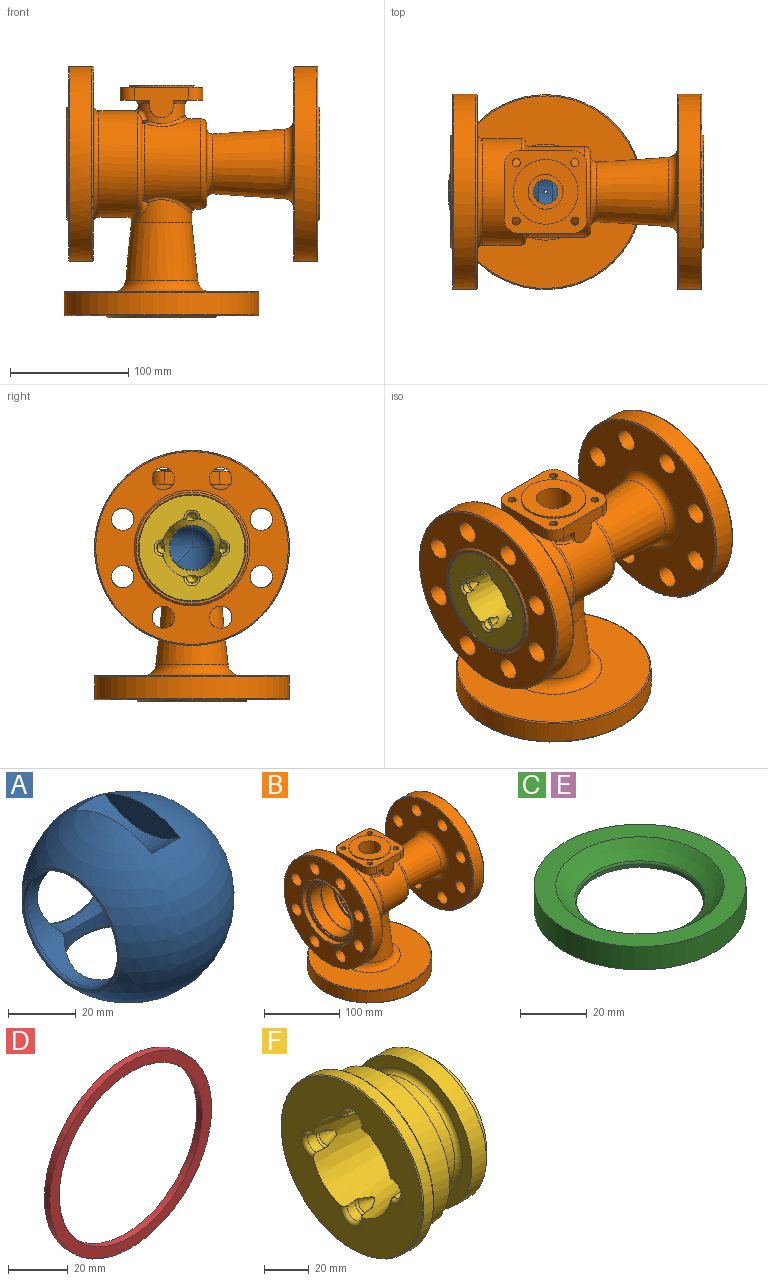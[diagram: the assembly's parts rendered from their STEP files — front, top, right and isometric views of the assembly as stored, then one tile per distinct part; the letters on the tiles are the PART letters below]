
ASSEMBLY  parts=6 mates=11
PART A: 15 faces, bbox 63x63x55.2 mm
  f0: sphere r=19mm, area 565.3mm2, adj f2,f3,f7,f14
  f1: cylinder r=25.4mm len=32.65mm, axis (1,0,0), area 413.6mm2, adj f4,f5,f6,f14
  f2: cylinder r=19mm len=38mm, axis (1,0,0), area 1522.5mm2, adj f0,f3,f7,f11,f14
  f3: cylinder r=19mm len=38mm, axis (0,1,0), area 1540.4mm2, adj f0,f2,f7,f10,f14
  f4: sphere r=31.5mm, area 7592mm2, adj f1,f5,f6,f9,f12,f13
  f5: plane 31.7x9.92mm, normal (1,0,0), area 213.9mm2, adj f1,f4
  f6: plane 31.7x9.92mm, normal (-1,0,0), area 213.9mm2, adj f1,f4
  f7: cylinder r=19mm len=38mm, axis (0,0,1), area 1543.1mm2, adj f0,f2,f3,f8
  f8: torus R=20mm, axis (0,0,1), area 103.9mm2, adj f7,f9
  f9: torus R=19.87mm, axis (0,0,-1), area 140.8mm2, adj f4,f8
  f10: torus R=20mm, axis (0,-1,0), area 103.9mm2, adj f3,f12
  f11: torus R=20mm, axis (1,0,0), area 185mm2, adj f2,f13
  f12: torus R=19.87mm, axis (0,1,0), area 140.8mm2, adj f4,f10
  f13: torus R=19.99mm, axis (-1,0,0), area 77.1mm2, adj f4,f11
  f14: cylinder r=1.5mm len=3mm, axis (0,0,-1), area 19.2mm2, adj f0,f1,f2,f3
PART B: 128 faces, bbox 239.3x194.7x235.4 mm
  f0: plane 163.1x163.1mm, normal (1,0,0), area 11081.7mm2, adj f41,f50,f114,f115,f116,f117,f118,f119
  f1: plane 163.1x163.1mm, normal (-1,0,0), area 14231.2mm2, adj f43,f51,f114,f115,f116,f117,f118,f119
  f2: plane 70x25mm, normal (0,0,-1), area 1229.7mm2, adj f9,f13,f14,f15,f16,f100,f104,f122
  f3: cylinder r=20mm len=40mm, axis (0,0,1), area 1013mm2, adj f75,f78,f81,f82,f100,f101,f102,f103
  f4: torus R=41mm, axis (1,0,0), area 611.2mm2, adj f18,f19,f75,f94
  f5: cylinder r=38.25mm len=76.5mm, axis (-1,0,0), area 7907mm2, adj f7,f47,f52,f73,f80,f81,f85,f86
  f6: plane 83.81x38.56mm, normal (1,0,0), area 59.6mm2, adj f7,f17,f79,f93
  f7: torus R=40.25mm, axis (1,0,0), area 238mm2, adj f5,f6,f80,f87
  f8: cylinder r=31.8mm len=63.6mm, axis (-1,0,0), area 9275.5mm2, adj f34,f35,f58,f69
  f9: plane 46x26mm, normal (0,1,0), area 763.1mm2, adj f2,f10,f16,f53,f55,f103,f104,f105
  f10: cylinder r=12mm len=12mm, axis (0,0,1), area 207.3mm2, adj f9,f11,f53,f55
  f11: plane 46x11mm, normal (-1,0,0), area 506mm2, adj f10,f12,f53,f55
  f12: cylinder r=12mm len=12mm, axis (0,0,1), area 207.3mm2, adj f11,f13,f53,f55
  f13: plane 46x26mm, normal (0,-1,0), area 763.1mm2, adj f2,f12,f14,f53,f55,f100,f101,f102
  f14: cylinder r=12mm len=12mm, axis (0,0,1), area 207.3mm2, adj f2,f13,f15,f55
  f15: plane 46x11mm, normal (1,0,0), area 506mm2, adj f2,f14,f16,f55
  f16: cylinder r=12mm len=12mm, axis (0,0,1), area 207.3mm2, adj f2,f9,f15,f55
  f17: torus R=41mm, axis (1,0,0), area 1154.6mm2, adj f6,f19,f82,f95
  f18: plane 67.81x22.56mm, normal (1,0,0), area 59.6mm2, adj f4,f52,f74,f88
  f19: cylinder r=45mm len=90mm, axis (-1,0,0), area 9132.6mm2, adj f4,f17,f78,f96,f99
  f20: plane 163.1x163.1mm, normal (1,0,0), area 10770.6mm2, adj f48,f99,f106,f107,f108,f109,f110,f111
  f21: cylinder r=82.55mm len=165.1mm, axis (-1,0,0), area 9699.3mm2, adj f48,f49
  f22: plane 163.1x163.1mm, normal (-1,0,0), area 11081.7mm2, adj f23,f49,f106,f107,f108,f109,f110,f111
  f23: cone r=47.4mm half-angle=45deg, axis (1,0,0), area 685.3mm2, adj f22,f24
  f24: plane 94.8x94.8mm, normal (-1,0,0), area 554.5mm2, adj f23,f25
  f25: cylinder r=45.5mm len=91mm, axis (-1,0,0), area 1989.8mm2, adj f24,f26
  f26: plane 91x91mm, normal (-1,0,0), area 1350.9mm2, adj f25,f27
  f27: cylinder r=40.5mm len=81mm, axis (-1,0,0), area 381.7mm2, adj f26,f28
  f28: plane 81x81mm, normal (-1,0,0), area 394.2mm2, adj f27,f29
  f29: cylinder r=38.92mm len=77.84mm, axis (-1,0,0), area 4646.3mm2, adj f28,f30
  f30: cone r=38.92mm half-angle=45deg, axis (-1,0,0), area 297.5mm2, adj f29,f31
  f31: cylinder r=38.05mm len=76.1mm, axis (-1,0,0), area 5094.7mm2, adj f30,f32
  f32: plane 76.1x76.1mm, normal (-1,0,0), area 980.5mm2, adj f31,f33
  f33: cylinder r=33.7mm len=67.4mm, axis (-1,0,0), area 603.5mm2, adj f32,f34
  f34: plane 67.4x67.4mm, normal (-1,0,0), area 391mm2, adj f8,f33
  f35: plane 63.6x63.6mm, normal (-1,0,0), area 1888.7mm2, adj f8,f36
  f36: cone r=20.25mm half-angle=30deg, axis (1,0,0), area 116.2mm2, adj f35,f37
  f37: torus R=20.1mm, axis (-1,0,0), area 152.4mm2, adj f36,f38
  f38: cylinder r=19.1mm len=38.2mm, axis (-1,0,0), area 1440.1mm2, adj f37,f39
  f39: cone r=19.1mm half-angle=3.8deg, axis (1,0,0), area 13140.1mm2, adj f38,f40
  f40: plane 94.8x94.8mm, normal (1,0,0), area 5031.6mm2, adj f39,f41
  f41: cone r=47.4mm half-angle=45deg, axis (-1,0,0), area 685.3mm2, adj f0,f40
  f42: cylinder r=82.55mm len=165.1mm, axis (-1,0,0), area 9699.3mm2, adj f50,f51
  f43: torus R=37.4mm, axis (-1,0,0), area 2451.4mm2, adj f1,f44
  f44: cone r=25.33mm half-angle=3.8deg, axis (1,0,0), area 10485mm2, adj f43,f45
  f45: torus R=30.32mm, axis (-1,0,0), area 1392.3mm2, adj f44,f46
  f46: plane 66.5x66.5mm, normal (1,0,0), area 585.9mm2, adj f45,f47
  f47: torus R=33.25mm, axis (-1,0,0), area 1797.9mm2, adj f5,f46
  f48: torus R=81.55mm, axis (1,0,0), area 811.1mm2, adj f20,f21
  f49: torus R=81.55mm, axis (-1,0,0), area 811.1mm2, adj f21,f22
  f50: torus R=81.55mm, axis (-1,0,0), area 811.1mm2, adj f0,f42
  f51: torus R=81.55mm, axis (1,0,0), area 811.1mm2, adj f1,f42
  f52: torus R=40.25mm, axis (1,0,0), area 238mm2, adj f5,f18,f73,f85
  f53: plane 70x25mm, normal (0,0,-1), area 1229.7mm2, adj f9,f10,f11,f12,f13,f101,f103,f123
  f54: cylinder r=27.45mm len=54.9mm, axis (0,0,1), area 258.7mm2, adj f55,f57
  f55: plane 70x70mm, normal (0,0,1), area 2263.9mm2, adj f9,f10,f11,f12,f13,f14,f15,f16
  f56: cylinder r=14.75mm len=29.5mm, axis (0,0,1), area 2177.9mm2, adj f57,f59
  f57: plane 54.9x54.9mm, normal (0,0,1), area 1683.7mm2, adj f54,f56
  f58: cylinder r=14.75mm len=29.5mm, axis (0,0,-1), area 832.8mm2, adj f8,f61
  f59: plane 29.5x29.5mm, normal (0,0,1), area 343.7mm2, adj f56,f60
  f60: cylinder r=10.4mm len=20.8mm, axis (0,0,-1), area 261.4mm2, adj f59,f61
  f61: plane 29.5x29.5mm, normal (0,0,-1), area 343.7mm2, adj f58,f60
  f62: plane 163x163mm, normal (0,0,1), area 15679.6mm2, adj f72,f97
  f63: cylinder r=82.5mm len=165mm, axis (0,0,1), area 9537.9mm2, adj f97,f98
  f64: plane 163x163mm, normal (0,0,-1), area 13749.1mm2, adj f65,f98
  f65: cone r=47.6mm half-angle=45deg, axis (0,0,1), area 665.4mm2, adj f64,f66
  f66: plane 92x92mm, normal (0,0,-1), area 4620.8mm2, adj f65,f67
  f67: cylinder r=25.4mm len=50.8mm, axis (0,0,1), area 3049.5mm2, adj f66,f68
  f68: cone r=19mm half-angle=6deg, axis (0,0,-1), area 8540.4mm2, adj f67,f69
  f69: cylinder r=19mm len=38mm, axis (0,0,1), area 2172.7mm2, adj f8,f68
  f70: cylinder r=25.5mm len=51mm, axis (0,0,1), area 1760.2mm2, adj f71,f86,f94,f95,f96
  f71: cone r=25.5mm half-angle=6deg, axis (0,0,-1), area 8766mm2, adj f70,f72
  f72: torus R=40.64mm, axis (0,0,1), area 3180.6mm2, adj f62,f71
  f73: bspline ~3.63x2.8mm, area 5.9mm2, adj f5,f52,f74,f76
  f74: cylinder r=3mm len=3.77mm, axis (0,0,1), area 2.4mm2, adj f18,f73,f75,f76
  f75: bspline ~11.75x11.14mm, area 70.4mm2, adj f3,f4,f74,f77,f78
  f76: bspline ~3.46x2.44mm, area 4.4mm2, adj f73,f74,f77,f81
  f77: bspline ~1.43x1.35mm, area 0.3mm2, adj f75,f76,f81
  f78: bspline ~23.01x6.08mm, area 84.3mm2, adj f3,f19,f75,f82
  f79: cylinder r=3mm len=3.77mm, axis (0,0,1), area 2.4mm2, adj f6,f80,f82,f83
  f80: bspline ~3.63x2.8mm, area 5.9mm2, adj f5,f7,f79,f83
  f81: bspline ~42.67x38.25mm, area 346.8mm2, adj f3,f5,f76,f77,f83,f84
  f82: bspline ~11.57x10.69mm, area 70.4mm2, adj f3,f17,f78,f79,f84
  f83: bspline ~3.46x2.44mm, area 4.4mm2, adj f79,f80,f81,f84
  f84: bspline ~1.43x1.35mm, area 0.3mm2, adj f81,f82,f83
  f85: bspline ~4.06x3.27mm, area 5.9mm2, adj f5,f52,f88,f89
  f86: bspline ~53.43x45.01mm, area 502.6mm2, adj f5,f70,f90,f91
  f87: bspline ~4.06x3.27mm, area 5.9mm2, adj f5,f7,f92,f93
  f88: cylinder r=4mm len=2.34mm, axis (0,0,1), area 1.2mm2, adj f18,f85,f94
  f89: bspline ~3.08x2.45mm, area 2.9mm2, adj f5,f85,f90,f94
  f90: bspline ~4.27x3.09mm, area 2.8mm2, adj f86,f89,f94
  f91: bspline ~4.26x3.08mm, area 2.8mm2, adj f86,f92,f95
  f92: bspline ~3.08x2.45mm, area 2.9mm2, adj f5,f87,f91,f95
  f93: cylinder r=4mm len=2.34mm, axis (0,0,1), area 1.2mm2, adj f6,f87,f95
  f94: bspline ~14.91x10.3mm, area 84mm2, adj f4,f70,f88,f89,f90,f96
  f95: bspline ~14.91x10.3mm, area 84mm2, adj f17,f70,f91,f92,f93,f96
  f96: bspline ~42.54x13.7mm, area 245mm2, adj f19,f70,f94,f95
  f97: torus R=81.5mm, axis (0,0,-1), area 810.7mm2, adj f62,f63
  f98: torus R=81.5mm, axis (0,0,-1), area 810.7mm2, adj f63,f64
  f99: torus R=50mm, axis (1,0,0), area 2310.3mm2, adj f19,f20
  f100: plane 18.21x5.53mm, normal (1,0,0), area 86.2mm2, adj f2,f3,f13,f102,f122
  f101: plane 18.21x5.53mm, normal (-1,0,0), area 86.2mm2, adj f3,f13,f53,f102,f123
  f102: cylinder r=10mm len=20mm, axis (0,-1,0), area 555.4mm2, adj f3,f13,f100,f101
  f103: plane 18.21x5.53mm, normal (-1,0,0), area 86.2mm2, adj f3,f9,f53,f105,f123
  f104: plane 18.21x5.53mm, normal (1,0,0), area 86.2mm2, adj f2,f3,f9,f105,f122
  f105: cylinder r=10mm len=20mm, axis (0,1,0), area 555.4mm2, adj f3,f9,f103,f104
  f106: cylinder r=9.5mm len=20.7mm, axis (-1,0,0), area 1235.6mm2, adj f20,f22
  f107: cylinder r=9.5mm len=20.7mm, axis (-1,0,0), area 1235.6mm2, adj f20,f22
  f108: cylinder r=9.5mm len=20.7mm, axis (-1,0,0), area 1235.6mm2, adj f20,f22
  f109: cylinder r=9.5mm len=20.7mm, axis (-1,0,0), area 1235.6mm2, adj f20,f22
  f110: cylinder r=9.5mm len=20.7mm, axis (-1,0,0), area 1235.6mm2, adj f20,f22
  f111: cylinder r=9.5mm len=20.7mm, axis (-1,0,0), area 1235.6mm2, adj f20,f22
  f112: cylinder r=9.5mm len=20.7mm, axis (-1,0,0), area 1235.6mm2, adj f20,f22
  f113: cylinder r=9.5mm len=20.7mm, axis (-1,0,0), area 1235.6mm2, adj f20,f22
  f114: cylinder r=9.5mm len=20.7mm, axis (1,0,0), area 1235.6mm2, adj f0,f1
  f115: cylinder r=9.5mm len=20.7mm, axis (1,0,0), area 1235.6mm2, adj f0,f1
  f116: cylinder r=9.5mm len=20.7mm, axis (1,0,0), area 1235.6mm2, adj f0,f1
  f117: cylinder r=9.5mm len=20.7mm, axis (1,0,0), area 1235.6mm2, adj f0,f1
  f118: cylinder r=9.5mm len=20.7mm, axis (1,0,0), area 1235.6mm2, adj f0,f1
  f119: cylinder r=9.5mm len=20.7mm, axis (1,0,0), area 1235.6mm2, adj f0,f1
  f120: cylinder r=9.5mm len=20.7mm, axis (1,0,0), area 1235.6mm2, adj f0,f1
  f121: cylinder r=9.5mm len=20.7mm, axis (1,0,0), area 1235.6mm2, adj f0,f1
  f122: torus R=23mm, axis (0,0,1), area 215.7mm2, adj f2,f3,f100,f104
  f123: torus R=23mm, axis (0,0,1), area 215.7mm2, adj f3,f53,f101,f103
  f124: cylinder r=3.4mm len=11mm, axis (0,0,1), area 235mm2, adj f2,f55
  f125: cylinder r=3.4mm len=11mm, axis (0,0,1), area 235mm2, adj f53,f55
  f126: cylinder r=3.4mm len=11mm, axis (0,0,1), area 235mm2, adj f53,f55
  f127: cylinder r=3.4mm len=11mm, axis (0,0,1), area 235mm2, adj f2,f55
PART C: 7 faces, bbox 63.4x63.4x8.5 mm
  f0: cylinder r=31.7mm len=63.4mm, axis (0,0,-1), area 1693mm2, adj f1,f6
  f1: plane 63.4x63.4mm, normal (0,0,-1), area 1347.4mm2, adj f0,f2
  f2: cone r=24mm half-angle=72.1deg, axis (0,0,-1), area 703.6mm2, adj f1,f3
  f3: cylinder r=19.05mm len=38.1mm, axis (0,0,-1), area 153.3mm2, adj f2,f4
  f4: torus R=20.05mm, axis (0,0,-1), area 117.9mm2, adj f3,f5
  f5: sphere r=34.85mm, area 1048.9mm2, adj f4,f6
  f6: plane 63.4x63.4mm, normal (0,0,1), area 1166.1mm2, adj f0,f5
PART D: 4 faces, bbox 76.5x2.6x76.5 mm
  f0: cylinder r=33.8mm len=67.6mm, axis (0,1,0), area 552.2mm2, adj f2,f3
  f1: cylinder r=38.25mm len=76.5mm, axis (0,1,0), area 624.9mm2, adj f2,f3
  f2: plane 76.5x76.5mm, normal (0,-1,0), area 1007.3mm2, adj f0,f1
  f3: plane 76.5x76.5mm, normal (0,1,0), area 1007.3mm2, adj f0,f1
PART E: same geometry as C
PART F: 41 faces, bbox 52.9x98.2x98.2 mm
  f0: cone r=25.4mm half-angle=7.9deg, axis (-1,0,0), area 5501.8mm2, adj f1,f12,f23,f24,f25,f26,f27,f29
  f1: plane 89.7x89.7mm, normal (-1,0,0), area 3988.9mm2, adj f0,f18,f37,f38,f39,f40
  f2: plane 75.94x75.94mm, normal (1,0,0), area 1012.1mm2, adj f3,f17
  f3: cylinder r=37.97mm len=75.94mm, axis (-1,0,0), area 2218.7mm2, adj f2,f4
  f4: plane 75.94x75.94mm, normal (-1,0,0), area 1297.2mm2, adj f3,f5
  f5: torus R=32.08mm, axis (-1,0,0), area 752.1mm2, adj f4,f6
  f6: cylinder r=29.57mm len=59.15mm, axis (-1,0,0), area 1501.4mm2, adj f5,f7
  f7: torus R=32.08mm, axis (-1,0,0), area 578.6mm2, adj f6,f8
  f8: cone r=40mm half-angle=70deg, axis (-1,0,0), area 2090.6mm2, adj f7,f9
  f9: cylinder r=40mm len=80mm, axis (-1,0,0), area 3081.8mm2, adj f8,f21
  f10: plane 89.7x89.7mm, normal (1,0,0), area 1782.9mm2, adj f20,f22
  f11: cylinder r=45.35mm len=90.7mm, axis (-1,0,0), area 1709.7mm2, adj f18,f22
  f12: cone r=19.1mm half-angle=45deg, axis (-1,0,0), area 85.1mm2, adj f0,f13
  f13: cylinder r=19.1mm len=38.2mm, axis (-1,0,0), area 1200.1mm2, adj f12,f14
  f14: torus R=19.79mm, axis (-1,0,0), area 105.8mm2, adj f13,f15
  f15: cone r=20mm half-angle=30deg, axis (-1,0,0), area 86.3mm2, adj f14,f16
  f16: plane 66.92x66.92mm, normal (1,0,0), area 2260.6mm2, adj f15,f17
  f17: cylinder r=33.46mm len=66.92mm, axis (-1,0,0), area 988.1mm2, adj f2,f16
  f18: cone r=44.85mm half-angle=45deg, axis (1,0,0), area 200.4mm2, adj f1,f11
  f19: cone r=42.68mm half-angle=60deg, axis (1,0,0), area 493.6mm2, adj f20,f21
  f20: cylinder r=38mm len=76mm, axis (-1,0,0), area 358.1mm2, adj f10,f19
  f21: torus R=39.5mm, axis (1,0,0), area 131.3mm2, adj f9,f19
  f22: torus R=44.85mm, axis (1,0,0), area 222.9mm2, adj f10,f11
  f23: cylinder r=5mm len=10mm, axis (-1,0,0), area 89.3mm2, adj f0,f33,f37
  f24: cylinder r=5mm len=10mm, axis (-1,0,0), area 89.3mm2, adj f0,f34,f38
  f25: cylinder r=5mm len=10mm, axis (-1,0,0), area 89.3mm2, adj f0,f35,f39
  f26: cylinder r=5mm len=10mm, axis (-1,0,0), area 89.3mm2, adj f0,f36,f40
  f27: cone r=0.87mm half-angle=30deg, axis (-1,0,0), area 86.8mm2, adj f0,f28,f36
  f28: sphere r=1mm, area 3.1mm2, adj f27
  f29: cone r=0.87mm half-angle=30deg, axis (-1,0,0), area 86.8mm2, adj f0,f30,f34
  f30: sphere r=1mm, area 3.1mm2, adj f29
  f31: cone r=5mm half-angle=30deg, axis (-1,0,0), area 91.6mm2, adj f0,f35
  f32: cone r=5mm half-angle=30deg, axis (-1,0,0), area 91.6mm2, adj f0,f33
  f33: torus R=2mm, axis (-1,0,0), area 27.7mm2, adj f0,f23,f32
  f34: torus R=2mm, axis (-1,0,0), area 27.7mm2, adj f0,f24,f29
  f35: torus R=2mm, axis (-1,0,0), area 27.7mm2, adj f0,f25,f31
  f36: torus R=2mm, axis (-1,0,0), area 27.7mm2, adj f0,f26,f27
  f37: torus R=7mm, axis (1,0,0), area 58.8mm2, adj f0,f1,f23
  f38: torus R=7mm, axis (1,0,0), area 58.8mm2, adj f0,f1,f24
  f39: torus R=7mm, axis (1,0,0), area 58.8mm2, adj f0,f1,f25
  f40: torus R=7mm, axis (1,0,0), area 58.8mm2, adj f0,f1,f26
PLACE A t=(5.78,-3.65,-8.97)mm
PLACE B t=(-74.56,-3.65,-9.04)mm fixed
PLACE C rot(axis=(0.48,-0.74,-0.48),107deg) t=(33.83,-3.65,-9.04)mm
PLACE D rot(axis=(0,0,1),90deg) t=(-27.52,-3.65,-9.04)mm
PLACE E rot(axis=(0,1,0),90deg) t=(-22.27,-3.65,-9.04)mm
PLACE F rot(axis=(1,0,0),0deg) t=(-74.6,-3.65,-9.04)mm
MATE planar B.f4 <-> F.f0  axis (-1,0,0) through (-74.56,-3.65,-9.04)mm
MATE cylindrical A.f14 <-> B.f56  axis (0,0,-1) through (5.78,-3.65,12.09)mm
MATE cylindrical B.f4 <-> F.f0  axis (-1,0,0) through (-24.92,-3.65,-9.04)mm
MATE planar C.f0 <-> B.f4  axis (1,0,0) through (33.83,-3.65,-9.04)mm
MATE cylindrical B.f4 <-> F.f0  axis (-1,0,0) through (-35.58,-3.65,-9.04)mm
MATE cylindrical C.f0 <-> B.f4  axis (-1,0,0) through (25.33,-3.65,-9.04)mm
MATE cylindrical E.f0 <-> F.f0  axis (-1,0,0) through (-22.27,-3.65,-9.04)mm
MATE planar E.f0 <-> F.f0  axis (-1,0,0) through (-22.27,-3.65,-9.04)mm
MATE cylindrical D.f0 <-> F.f0  axis (1,0,0) through (-24.92,-3.65,-9.04)mm
MATE planar D.f1 <-> B.f4  axis (1,0,0) through (-24.92,-3.65,-9.04)mm
MATE parallel B.f11 <-> A.f5  axis (-1,0,0) through (-29.22,-3.65,55.96)mm
